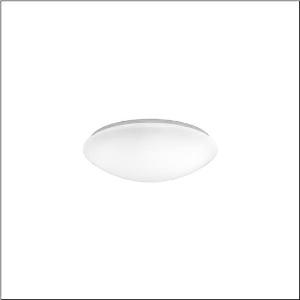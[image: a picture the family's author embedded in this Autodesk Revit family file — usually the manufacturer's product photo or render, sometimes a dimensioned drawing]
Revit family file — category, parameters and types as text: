
# Revit family: round_31_b_5pja010001a
name_source: partatom
category: Lighting Fixtures
units: mm (PartAtom-declared; Revit-internal decimal feet)

## family parameters
Cut with Voids When Loaded = No
Host = Face
Light Source = No
Part Type = Normal
Room Calculation Point = No
Round Connector Dimension = Use Diameter
Shared = No

## types (1)
- Round 31 B (1 x LED, 1800 lm, 15 W, 3000K)
    Apparent Load = 15 VA
    CIE Flux Codes = 42 71 89 88 100
    Color Rendering = 80
    Color Temperature = 3000K
    Default Elevation = 1800 mm  [stored 5.90551 ft]
    Description = Round 31 B, wall and ceiling luminaire, primary optical cover: enclosure, of PMMA, light emission: direct distribution, primary light characteristic: symmetric, installation type: surface-mounted, LED, rated luminous flux: 1.800lm, luminous efficacy: 120lm/W, light colour: 830, colour temperature: 3000K, with terminal, 3-pole, max. 2.5mm², mains connection: 230V, AC, 50/60Hz, rated input power: 15W, luminaire housing, round, of steel, white, diameter: 290mm, height: 85mm, protection rating (complete): IP40, insulation class (complete): insulation class I (protective earthing), certification: CE, impact resistance: IK02, permissible operating ambient temperature: -20..+25°C, packaging unit: 1 piece
    Height = 85 mm
    Lamp = 1 x LED
    Lamp Light Flux = 1800 lm
    Lamp Power = 15 W
    Lamp count = 1
    Length = 290 mm
    Luminous efficacy = 120 lm/W
    Manufacturer = Siteco
    ModVariant = No
    Model = 5PJA010001A
    Mounting Place = Ceiling
    Mounting Type = Surface mounted
    Number of Poles = 1
    OnlyDefault = Yes
    Power Factor = 1
    Product Name = Round 31 B
    Product group = wall and ceiling luminaire
    ProductGroupID = 301
    Protection Class = Protection class I
    Protection Degree = IP 40
    RLX_Detail_Level = 1
    RLX_Emergency_Light_Flux = 0 lm
    RLX_Emergency_Type = 0
    RLX_Emergency_Type_DB = No
    RlxData = <blob elided: 9241 chars, md5=dbd689bd>
    Socket = socket
    Standby Power = 0 W
    System Light Flux = 1800 lm
    System Power = 15 W
    Type Comments = Product without accessories
    Type Image = l_1258346.jpg
    URL = http://relux.com
    VarID = ---
    Voltage = 0 V
    Weight = 0.00 kg
    Width = 0 mm  [stored 0 ft]

note: [stored X ft] marks values corroborated as IEEE doubles in the binary element streams (Revit-internal decimal feet)

## geometry (parser evidence)
native form markers: Sweep x11
no freeform markers — native parametric forms only
